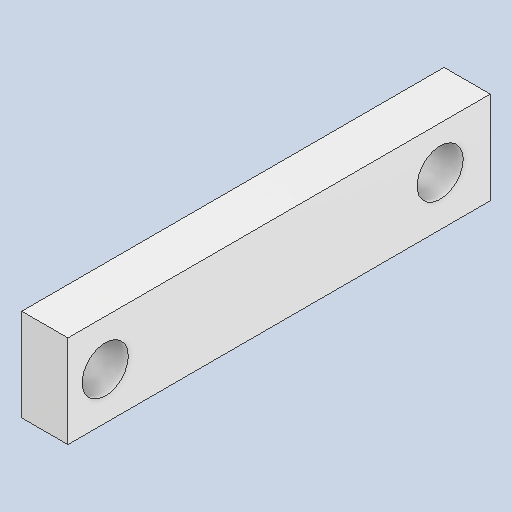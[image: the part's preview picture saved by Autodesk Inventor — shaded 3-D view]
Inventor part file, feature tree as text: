
AUTODESK INVENTOR PART (.ipt)
format: ipt  version: 2023 (Build 270158000, 158)  size: 212,480 bytes
history: native  units: in
note: dims shown in document units (in); Inventor stores cm internally (conversion verified against a paired STEP export)
features: sketch x3, hole x2, extrude x1
ambient origin geometry x8: Origin, YZ Plane, XZ Plane, XY Plane, X Axis, Y Axis, Z Axis, Center Point
bodies: Solid1 (feature_tree)
feature tree (6):
  extrude  "Extrusion1"  Depth=0.3937in TaperAngle=0.0deg
  hole  "Hole1"  [1 undecoded]
  hole  "Hole2"  [1 undecoded]
  sketch  "Sketch1"  dims[d1=0.7874in d2=0.3937in d3=0.0in]
  sketch  "Sketch2"  dims[d4=0.3937in d5=0.2362in d6=0.1575in d7=0.0787in d8=90.0deg d9=0.315in d10=0.8108in]
  sketch  "Sketch3"  dims[d11=0.3937in d12=0.2362in d13=0.1575in d14=0.0787in d15=90.0deg d16=0.315in d17=0.8108in]
note: 2 required parameter values undecoded (feature->parameter linkage not recoverable at this tier; creation-order binding heuristic only, values carry confidence <= 0.55)
